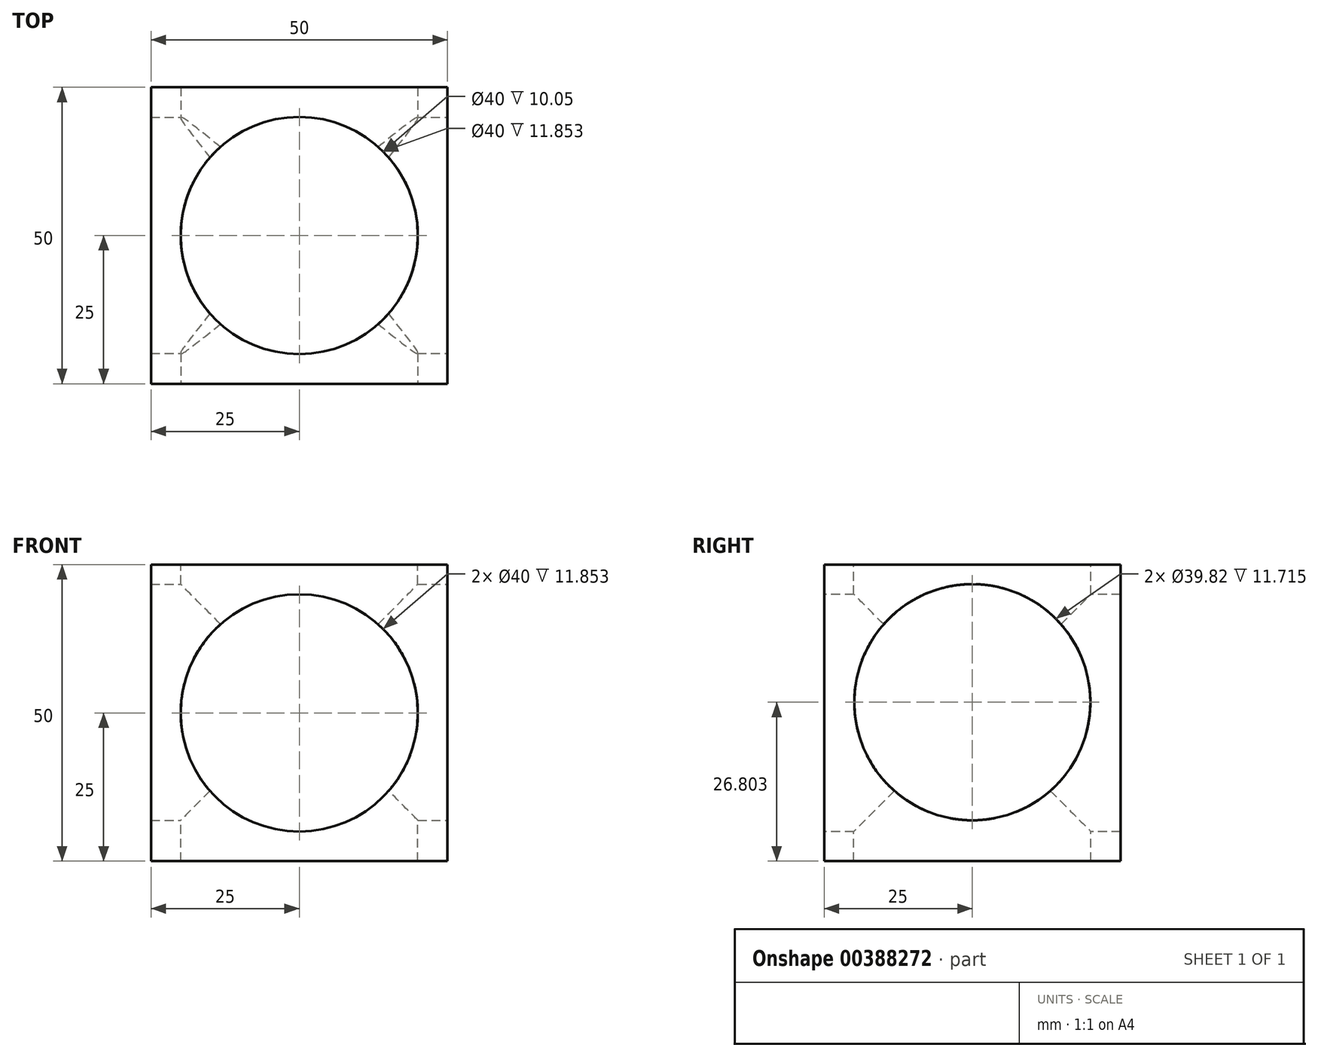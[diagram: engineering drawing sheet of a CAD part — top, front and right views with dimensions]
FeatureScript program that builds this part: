
annotation { "Feature Type Name" : "Feature", "Feature Type Description" : "" }
export const myFeature = defineFeature(function(context is Context, id is Id, definition is map)
    precondition{}
    {
        {
            var Q0;
            Q0=qCreatedBy(makeId("Top.planeOp"),FACE);
            var sketch = newSketch(context, id + "F0", { "sketchPlane" : qUnion([Q0])});
            skLineSegment(sketch, "E0.bottom", {"start": v(25, -25) * mm, "end": v(-25, -25) * mm});
            skLineSegment(sketch, "E0.top", {"start": v(25, 25) * mm, "end": v(-25, 25) * mm});
            skLineSegment(sketch, "E0.left", {"start": v(25, -25) * mm, "end": v(25, 25) * mm});
            skLineSegment(sketch, "E0.right", {"start": v(-25, -25) * mm, "end": v(-25, 25) * mm});
            skPoint(sketch, "E0.middle", {"position": v(0, 0) * mm});
            skSolve(sketch);
        }
        {
            var Q0;
            Q0 = qSketchRegion(id + "F0", true);
            extrude(context, id + "F1", {"entities" : qUnion([Q0]), "depth" : 50 * mm});
        }
        {
            var Q0;
            Q0=makeQuery(id+"F1.opExtrude","CAP_FACE",FACE,{"disambiguationData":[OSD([sQuery(id+"F0.wireOp",EDGE,"E0.bottom"),sQuery(id+"F0.wireOp",EDGE,"E0.top"),sQuery(id+"F0.wireOp",EDGE,"E0.left"),sQuery(id+"F0.wireOp",EDGE,"E0.right")])],"isStart":false});
            var sketch = newSketch(context, id + "F2", { "sketchPlane" : qUnion([Q0])});
            skCircle(sketch, "E1", {"center": v(0, 0) * mm, "radius": 20 * mm});
            skSolve(sketch);
        }
        {
            var Q0;
            Q0=makeQuery(id+"F2.imprint","IMPRINT",FACE,{"disambiguationData":[TD([[makeQuery(id+"F2.imprint","IMPRINT",EDGE,{"derivedFrom":sQuery(id+"F2.wireOp",EDGE,"E1")}),1.0]])]});
            extrude(context, id + "F3", {"entities" : qUnion([Q0]), "operationType" : NewBodyOperationType.REMOVE, "endBound" : BoundingType.THROUGH_ALL, "oppositeDirection" : true, "depth" : 25 * mm});
        }
        {
            var Q0;
            Q0=makeQuery(id+"F1.opExtrude","SWEPT_FACE",FACE,{"disambiguationData":[OSD([sQuery(id+"F0.wireOp",EDGE,"E0.bottom")])]});
            var sketch = newSketch(context, id + "F4", { "sketchPlane" : qUnion([Q0])});
            skCircle(sketch, "E2", {"center": v(0, 25) * mm, "radius": 20 * mm});
            skSolve(sketch);
        }
        {
            var Q0;
            Q0=makeQuery(id+"F4.imprint","IMPRINT",FACE,{"disambiguationData":[TD([[makeQuery(id+"F4.imprint","IMPRINT",EDGE,{"derivedFrom":sQuery(id+"F4.wireOp",EDGE,"E2")}),1.0]])]});
            extrude(context, id + "F5", {"entities" : qUnion([Q0]), "operationType" : NewBodyOperationType.REMOVE, "endBound" : BoundingType.THROUGH_ALL, "oppositeDirection" : true, "depth" : 40 * mm});
        }
        {
            var Q0;
            Q0=makeQuery(id+"F1.opExtrude","SWEPT_FACE",FACE,{"disambiguationData":[OSD([sQuery(id+"F0.wireOp",EDGE,"E0.left")])]});
            var sketch = newSketch(context, id + "F6", { "sketchPlane" : qUnion([Q0])});
            skCircle(sketch, "E3", {"center": v(0, 26.8) * mm, "radius": 19.9 * mm});
            skSolve(sketch);
        }
        {
            var Q0;
            Q0=makeQuery(id+"F6.imprint","IMPRINT",FACE,{"disambiguationData":[TD([[makeQuery(id+"F6.imprint","IMPRINT",EDGE,{"derivedFrom":sQuery(id+"F6.wireOp",EDGE,"E3")}),1.0]])]});
            extrude(context, id + "F7", {"entities" : qUnion([Q0]), "operationType" : NewBodyOperationType.REMOVE, "endBound" : BoundingType.THROUGH_ALL, "oppositeDirection" : true, "depth" : 25 * mm});
        }
    });
